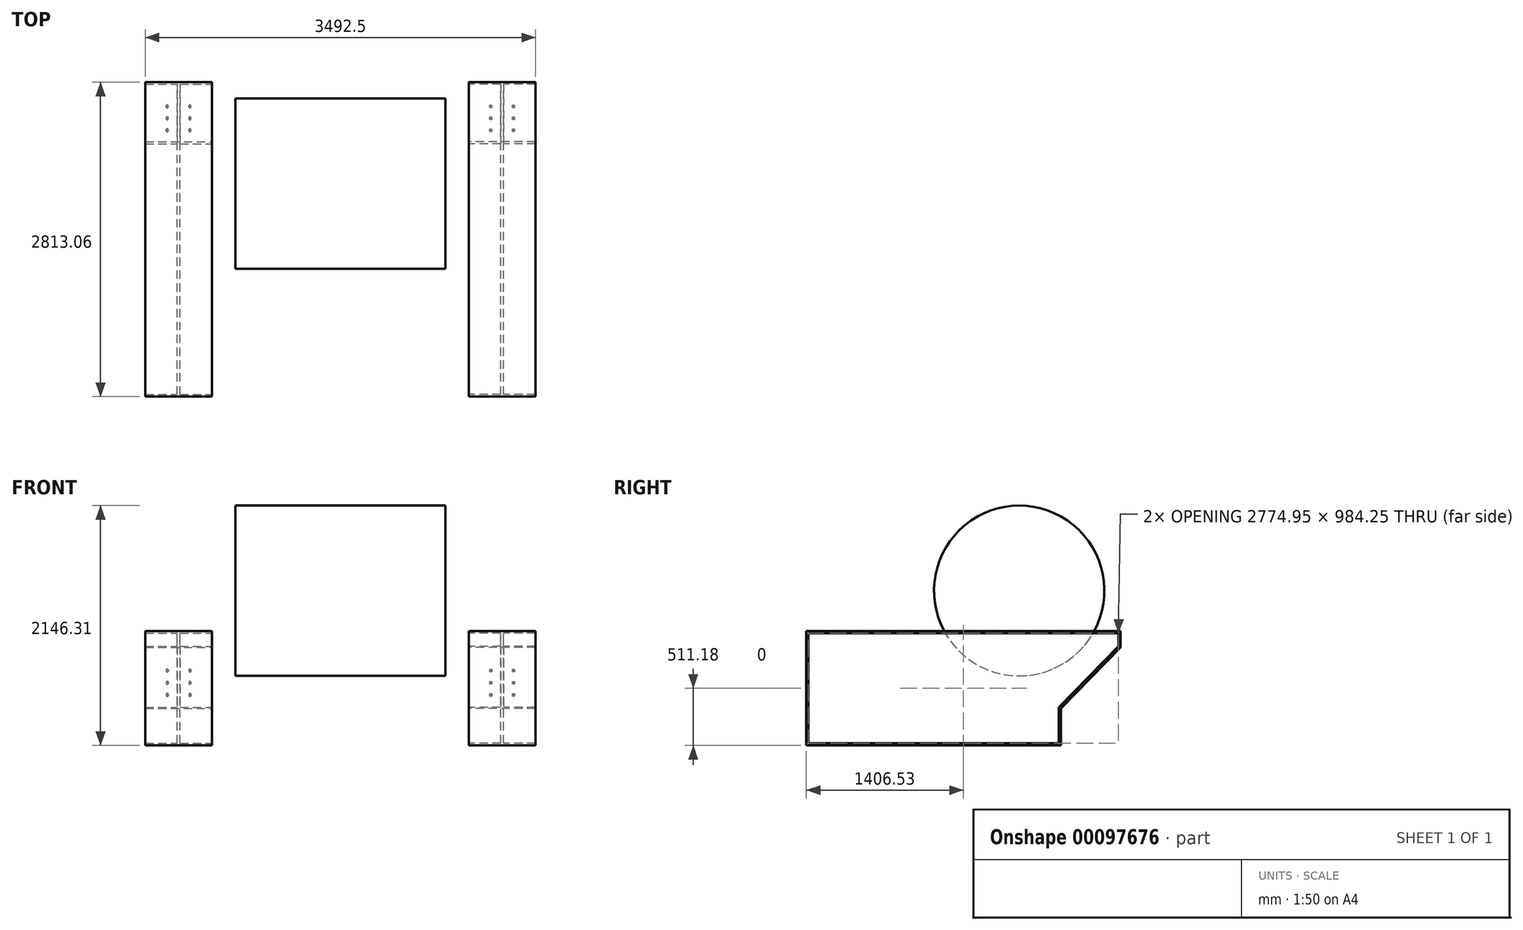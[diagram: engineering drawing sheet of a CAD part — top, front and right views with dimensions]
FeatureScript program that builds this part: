
annotation { "Feature Type Name" : "Feature", "Feature Type Description" : "" }
export const myFeature = defineFeature(function(context is Context, id is Id, definition is map)
    precondition{}
    {
        {
            var Q0;
            Q0=qCreatedBy(makeId("Right.planeOp"),FACE);
            var sketch = newSketch(context, id + "F0", { "sketchPlane" : qUnion([Q0])});
            skLineSegment(sketch, "E0.bottom", {"start": v(-1406.52, -511.18) * mm, "end": v(873.13, -511.18) * mm});
            skLineSegment(sketch, "E0.top", {"start": v(-1406.52, 511.17) * mm, "end": v(1406.53, 511.17) * mm});
            skLineSegment(sketch, "E0.left", {"start": v(-1406.52, -511.18) * mm, "end": v(-1406.52, 511.17) * mm});
            skLineSegment(sketch, "E0.right", {"start": v(1406.53, 367.1) * mm, "end": v(1406.53, 511.17) * mm});
            skPoint(sketch, "E0.middle", {"position": v(0, 0) * mm});
            skLineSegment(sketch, "E1.0", {"start": v(873.13, -511.18) * mm, "end": v(873.13, -179) * mm});
            skLineSegment(sketch, "E2", {"start": v(1406.53, 367.1) * mm, "end": v(873.13, -179) * mm});
            skPoint(sketch, "E3.orphan", {"position": v(1406.53, -511.18) * mm});
            skLineSegment(sketch, "E4.0", {"start": v(-1387.47, -492.13) * mm, "end": v(-1387.47, 492.12) * mm});
            skLineSegment(sketch, "E4.1", {"start": v(1387.48, 374.87) * mm, "end": v(1387.48, 492.12) * mm});
            skLineSegment(sketch, "E4.2", {"start": v(1387.48, 374.87) * mm, "end": v(854.08, -171.23) * mm});
            skLineSegment(sketch, "E4.3", {"start": v(-1387.47, 492.12) * mm, "end": v(1387.48, 492.12) * mm});
            skLineSegment(sketch, "E4.4", {"start": v(854.08, -492.13) * mm, "end": v(854.08, -171.23) * mm});
            skLineSegment(sketch, "E4.5", {"start": v(-1387.47, -492.13) * mm, "end": v(854.08, -492.13) * mm});
            skSolve(sketch);
        }
        {
            var Q0;
            Q0 = qSketchRegion(id + "F0", true);
            extrude(context, id + "F1", {"entities" : qUnion([Q0]), "endBound" : BoundingType.SYMMETRIC, "depth" : 596.9 * mm});
        }
        {
            var Q0;
            Q0=makeQuery(id+"F0.imprint","IMPRINT",FACE,{"disambiguationData":[TD([[makeQuery(id+"F0.imprint","IMPRINT",EDGE,{"derivedFrom":sQuery(id+"F0.wireOp",EDGE,"E4.0")}),-1.0]])]});
            extrude(context, id + "F2", {"entities" : qUnion([Q0]), "operationType" : NewBodyOperationType.ADD, "endBound" : BoundingType.SYMMETRIC, "depth" : 25.4 * mm});
        }
        {
            var Q0;
            Q0=makeQuery(id+"F1.opExtrude","CAP_FACE",FACE,{"disambiguationData":[OSD([sQuery(id+"F0.wireOp",EDGE,"E0.bottom"),sQuery(id+"F0.wireOp",EDGE,"E0.top"),sQuery(id+"F0.wireOp",EDGE,"E0.left"),sQuery(id+"F0.wireOp",EDGE,"E0.right"),sQuery(id+"F0.wireOp",EDGE,"E1.0"),sQuery(id+"F0.wireOp",EDGE,"E2"),sQuery(id+"F0.wireOp",EDGE,"E4.0"),sQuery(id+"F0.wireOp",EDGE,"E4.1"),sQuery(id+"F0.wireOp",EDGE,"E4.2"),sQuery(id+"F0.wireOp",EDGE,"E4.3"),sQuery(id+"F0.wireOp",EDGE,"E4.4"),sQuery(id+"F0.wireOp",EDGE,"E4.5")])],"isStart":false});
            cPlane(context, id + "F3", {"entities" : qUnion([Q0]), "cplaneType" : CPlaneType.OFFSET, "offset" : 1746.25 * mm, "oppositeDirection" : true, "width" : 152.4 * mm, "height" : 152.4 * mm});
        }
        {
            var Q0;
            Q0=makeQuery(id+"F1.opExtrude","CAP_FACE",FACE,{"disambiguationData":[OSD([sQuery(id+"F0.wireOp",EDGE,"E0.bottom"),sQuery(id+"F0.wireOp",EDGE,"E0.top"),sQuery(id+"F0.wireOp",EDGE,"E0.left"),sQuery(id+"F0.wireOp",EDGE,"E0.right"),sQuery(id+"F0.wireOp",EDGE,"E1.0"),sQuery(id+"F0.wireOp",EDGE,"E2"),sQuery(id+"F0.wireOp",EDGE,"E4.0"),sQuery(id+"F0.wireOp",EDGE,"E4.1"),sQuery(id+"F0.wireOp",EDGE,"E4.2"),sQuery(id+"F0.wireOp",EDGE,"E4.3"),sQuery(id+"F0.wireOp",EDGE,"E4.4"),sQuery(id+"F0.wireOp",EDGE,"E4.5")])],"isStart":false});
            var sketch = newSketch(context, id + "F4", { "sketchPlane" : qUnion([Q0])});
            skLineSegment(sketch, "E5.0", {"start": v(-1406.52, 511.17) * mm, "end": v(1547.24, 511.17) * mm});
            skLineSegment(sketch, "E6.0", {"start": v(1547.24, 511.18) * mm, "end": v(873.13, -179) * mm});
            skPoint(sketch, "E7.orphan", {"position": v(1406.53, 511.17) * mm});
            skPoint(sketch, "E8.orphan", {"position": v(1406.53, 367.1) * mm});
            skSolve(sketch);
        }
        {
            var Q0;
            Q0 = qSketchRegion(id + "F4", true);
            var Q1;
            {var subQ1=makeQuery(id+"F1.opExtrude","CAP_EDGE",EDGE,{"disambiguationData":[OSD([sQuery(id+"F0.wireOp",EDGE,"E0.right")])],"isStart":false});Q1=makeQuery(id+"F4.imprint","IMPRINT",FACE,{"disambiguationData":[TD([[makeQuery(id+"F4.imprint","IMPRINT",EDGE,{"derivedFrom":subQ1}),-1.0]])]});}
            extrude(context, id + "F5", {"entities" : qUnion([Q0, Q1]), "depth" : 152.4 * mm});
        }
        {
            var Q0;
            Q0=makeQuery(id+"F1.opExtrude","SWEPT_FACE",FACE,{"disambiguationData":[OSD([sQuery(id+"F0.wireOp",EDGE,"E2")])]});
            var sketch = newSketch(context, id + "F6", { "sketchPlane" : qUnion([Q0])});
            skLineSegment(sketch, "E9.0", {"start": v(-450.85, 1446.8) * mm, "end": v(-298.45, 1446.8) * mm, "construction": true});
            skLineSegment(sketch, "E10.0", {"start": v(-298.45, 1348.48) * mm, "end": v(298.45, 1348.48) * mm, "construction": true});
            skLineSegment(sketch, "E11", {"start": v(-298.45, 1446.8) * mm, "end": v(334.03, 1446.8) * mm, "construction": true});
            skLineSegment(sketch, "E12", {"start": v(0, 1348.48) * mm, "end": v(0, 155.59) * mm, "construction": true});
            skPoint(sketch, "E12.endSnap0", {"position": v(0, 1348.48) * mm});
            skLineSegment(sketch, "E13.0", {"start": v(-298.45, 945.15) * mm, "end": v(334.03, 945.15) * mm, "construction": true});
            skLineSegment(sketch, "E14.0", {"start": v(-298.45, 792.75) * mm, "end": v(334.03, 792.75) * mm, "construction": true});
            skLineSegment(sketch, "E15.0", {"start": v(-298.45, 640.35) * mm, "end": v(334.03, 640.35) * mm, "construction": true});
            skLineSegment(sketch, "E16.0", {"start": v(-101.6, 1348.48) * mm, "end": v(-101.6, 155.59) * mm, "construction": true});
            skLineSegment(sketch, "E17.0", {"start": v(101.6, 1348.48) * mm, "end": v(101.6, 155.59) * mm, "construction": true});
            skLineSegment(sketch, "E18.0", {"start": v(292.1, 488.4) * mm, "end": v(292.1, 1239.07) * mm, "construction": true});
            skLineSegment(sketch, "E18.1", {"start": v(-292.1, 488.4) * mm, "end": v(292.1, 488.4) * mm, "construction": true});
            skLineSegment(sketch, "E18.2", {"start": v(-292.1, 1239.07) * mm, "end": v(-292.1, 488.4) * mm, "construction": true});
            skLineSegment(sketch, "E18.3", {"start": v(292.1, 1239.07) * mm, "end": v(-292.1, 1239.07) * mm, "construction": true});
            skPoint(sketch, "E19", {"position": v(-101.6, 945.15) * mm});
            skPoint(sketch, "E20", {"position": v(-101.6, 792.75) * mm});
            skPoint(sketch, "E21", {"position": v(-101.6, 640.35) * mm});
            skPoint(sketch, "E22", {"position": v(101.6, 640.35) * mm});
            skPoint(sketch, "E23", {"position": v(101.6, 792.75) * mm});
            skPoint(sketch, "E24", {"position": v(101.6, 945.15) * mm});
            skSolve(sketch);
        }
        {
            var Q0;
            Q0=sQuery(id+"F6.wireOp",VERTEX,"E21");
            var Q1;
            Q1=sQuery(id+"F6.wireOp",VERTEX,"E20");
            var Q2;
            Q2=sQuery(id+"F6.wireOp",VERTEX,"E19");
            var Q3;
            Q3=sQuery(id+"F6.wireOp",VERTEX,"E24");
            var Q4;
            Q4=sQuery(id+"F6.wireOp",VERTEX,"E23");
            var Q5;
            Q5=sQuery(id+"F6.wireOp",VERTEX,"E22");
            var Q6;
            Q6=makeQuery(id+"F1.opExtrude","SWEPT_BODY",BODY,{"disambiguationData":[OSD([sQuery(id+"F0.wireOp",EDGE,"E0.bottom"),sQuery(id+"F0.wireOp",EDGE,"E0.top"),sQuery(id+"F0.wireOp",EDGE,"E0.left"),sQuery(id+"F0.wireOp",EDGE,"E0.right"),sQuery(id+"F0.wireOp",EDGE,"E1.0"),sQuery(id+"F0.wireOp",EDGE,"E2"),sQuery(id+"F0.wireOp",EDGE,"E4.0"),sQuery(id+"F0.wireOp",EDGE,"E4.1"),sQuery(id+"F0.wireOp",EDGE,"E4.2"),sQuery(id+"F0.wireOp",EDGE,"E4.3"),sQuery(id+"F0.wireOp",EDGE,"E4.4"),sQuery(id+"F0.wireOp",EDGE,"E4.5")])]});
            hole(context, id + "F7", {"style" : HoleStyle.SIMPLE, "endStyle" : HoleEndStyle.BLIND, "holeDiameter" : 17.46 * mm, "holeDepth" : 25.4 * mm, "locations" : qUnion([Q0, Q1, Q2, Q3, Q4, Q5]), "scope" : qUnion([Q6])});
        }
        {
            var Q0;
            Q0=makeQuery(id+"F5.opExtrude","SWEPT_BODY",BODY,{"disambiguationData":[OSD([sQuery(id+"F0.wireOp",EDGE,"E0.right"),sQuery(id+"F4.wireOp",EDGE,"E5.0"),sQuery(id+"F4.wireOp",EDGE,"E6.0")])]});
            deleteBodies(context, id + "F8", {"entities" : qUnion([Q0])});
        }
        {
            var Q0;
            Q0=makeQuery(id+"F1.opExtrude","SWEPT_BODY",BODY,{"disambiguationData":[OSD([sQuery(id+"F0.wireOp",EDGE,"E0.bottom"),sQuery(id+"F0.wireOp",EDGE,"E0.top"),sQuery(id+"F0.wireOp",EDGE,"E0.left"),sQuery(id+"F0.wireOp",EDGE,"E0.right"),sQuery(id+"F0.wireOp",EDGE,"E1.0"),sQuery(id+"F0.wireOp",EDGE,"E2"),sQuery(id+"F0.wireOp",EDGE,"E4.0"),sQuery(id+"F0.wireOp",EDGE,"E4.1"),sQuery(id+"F0.wireOp",EDGE,"E4.2"),sQuery(id+"F0.wireOp",EDGE,"E4.3"),sQuery(id+"F0.wireOp",EDGE,"E4.4"),sQuery(id+"F0.wireOp",EDGE,"E4.5")])]});
            var Q1;
            Q1=qCreatedBy(id+"F3.planeOp",FACE);
            mirror(context, id + "F9", {"entities" : qUnion([Q0]), "mirrorPlane" : qUnion([Q1])});
        }
        {
            var Q0;
            Q0=qCreatedBy(id+"F3.planeOp",FACE);
            var sketch = newSketch(context, id + "F10", { "sketchPlane" : qUnion([Q0])});
            skLineSegment(sketch, "E25.0", {"start": v(-1406.52, -511.18) * mm, "end": v(-1406.52, 511.17) * mm, "construction": true});
            skLineSegment(sketch, "E26.0", {"start": v(-1406.52, -511.18) * mm, "end": v(873.13, -511.18) * mm, "construction": true});
            skLineSegment(sketch, "E27.0", {"start": v(-1406.52, 873.12) * mm, "end": v(873.13, 873.12) * mm, "construction": true});
            skLineSegment(sketch, "E28.0", {"start": v(498.48, -511.18) * mm, "end": v(498.48, 873.12) * mm, "construction": true});
            skCircle(sketch, "E29", {"center": v(498.48, 873.12) * mm, "radius": 762 * mm});
            skSolve(sketch);
        }
        {
            var Q0;
            Q0 = qSketchRegion(id + "F10", true);
            extrude(context, id + "F11", {"entities" : qUnion([Q0]), "endBound" : BoundingType.SYMMETRIC, "depth" : 1879.6 * mm});
        }
    });
